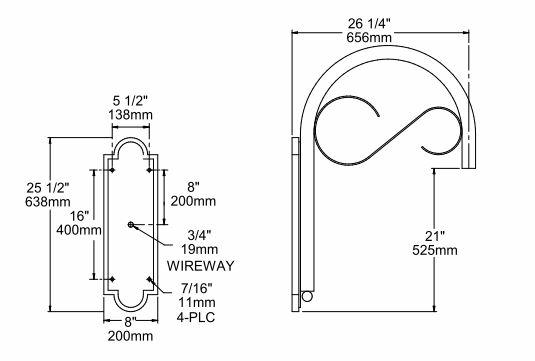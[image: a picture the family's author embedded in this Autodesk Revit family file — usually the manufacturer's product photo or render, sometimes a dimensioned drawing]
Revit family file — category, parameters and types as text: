
# Revit family: UCL
name_source: partatom
category: Lighting Fixtures
revit_build: Autodesk Revit MEP 2012 (Build: 20110309_2315(x64)
units: mm (PartAtom-declared; Revit-internal decimal feet)

## types (1)
- 30" Ø, UCL H2 250MH
    Absolute Lumens = 21000 lm
    Apparent Load = 250 VA
    Architectural Design Manual = http://cdn.aal.net
    Assembly Code = D5020200
    Bell Housing Radius = 15 "
    Bell Material = Stainless Steel-AAL-Horizontal Grain, Brushed Natural
    Default Elevation = 0 "
    Description = Lighting Fixture
    Frequency = 60 Hz
    Full Load Current = 1 A
    Glass Material = Glass-AAL-Acrylic
    Housing Height = 26.7 "
    Housing Material = Aluminum-AAL-Antique Green
    Housing Radius = 5.3 "
    LEED = www.usgbc.org
    Lamp = 250 WATT MOG BASE CLEAR ED-28 MH LAMP
    Load Classification = Lighting
    Manufacturer = Architectural Area Lighting
    MasterFormat Number = 26.56.29
    MasterFormat Title = Area Lighting
    Model = 30" Ø, UCL H2 250MH
    Note Text = LF
    Note Visible = Yes
    Number of Poles = 1
    OmniClass Number = 23.80.70.14.11.14
    OmniClass Title = Post-Top Lighting
    Photometric Web = Web UCL : UCL-T3-56LED-3K-450
    Power Factor = 1
    Revision Date = 02/22/2010
    Series = Universe
    URL = www.aal.net
    Voltage = 120 V
    Wattage Comments = 250MH BALLAST

## geometry (parser evidence)
native form markers: Blend x46, Sweep x39
no freeform markers — native parametric forms only
